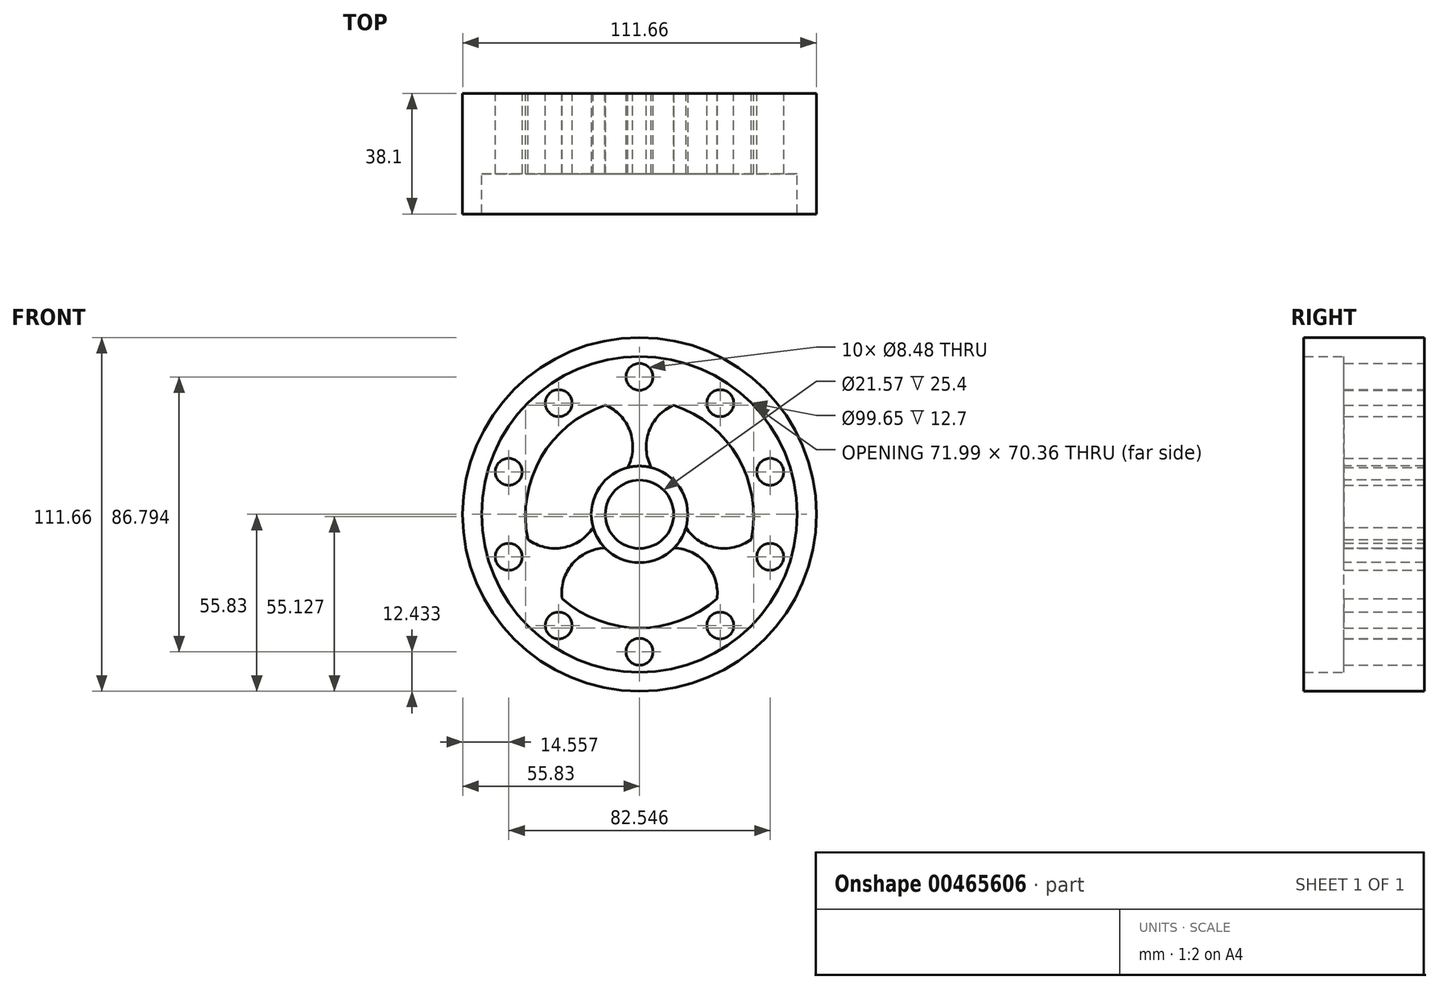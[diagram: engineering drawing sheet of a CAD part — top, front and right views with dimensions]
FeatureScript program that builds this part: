
annotation { "Feature Type Name" : "Feature", "Feature Type Description" : "" }
export const myFeature = defineFeature(function(context is Context, id is Id, definition is map)
    precondition{}
    {
        {
            var Q0;
            Q0=qCreatedBy(makeId("Front.planeOp"),FACE);
            var sketch = newSketch(context, id + "F0", { "sketchPlane" : qUnion([Q0])});
            skCircle(sketch, "E0", {"center": v(0, 0) * mm, "radius": 50.46 * mm});
            skCircle(sketch, "E1", {"center": v(0, 43.4) * mm, "radius": 4.24 * mm});
            skCircle(sketch, "E2.1.0", {"center": v(-25.5, 35.1) * mm, "radius": 4.24 * mm});
            skCircle(sketch, "E2.2.0", {"center": v(-41.27, 13.41) * mm, "radius": 4.24 * mm});
            skCircle(sketch, "E2.3.0", {"center": v(-41.27, -13.41) * mm, "radius": 4.24 * mm});
            skCircle(sketch, "E2.4.0", {"center": v(-25.5, -35.1) * mm, "radius": 4.24 * mm});
            skCircle(sketch, "E2.5.0", {"center": v(0, -43.4) * mm, "radius": 4.24 * mm});
            skCircle(sketch, "E2.6.0", {"center": v(25.5, -35.1) * mm, "radius": 4.24 * mm});
            skCircle(sketch, "E2.7.0", {"center": v(41.27, -13.41) * mm, "radius": 4.24 * mm});
            skCircle(sketch, "E2.8.0", {"center": v(41.27, 13.41) * mm, "radius": 4.24 * mm});
            skCircle(sketch, "E2.9.0", {"center": v(25.5, 35.1) * mm, "radius": 4.24 * mm});
            skArc(sketch, "E3", {"start": v(-3.72, 14.78) * mm, "mid": v(-2.95, 26.16) * mm, "end": v(-10.78, 34.48) * mm});
            skArc(sketch, "E4.MirrorCS", {"start": v(3.72, 14.78) * mm, "mid": v(2.95, 26.16) * mm, "end": v(10.78, 34.48) * mm});
            skCircle(sketch, "E5", {"center": v(0, 0) * mm, "radius": 15.24 * mm});
            skArc(sketch, "E6.1.0", {"start": v(-10.94, -10.6) * mm, "mid": v(-21.18, -15.64) * mm, "end": v(-24.47, -26.57) * mm});
            skArc(sketch, "E6.1.1", {"start": v(-14.65, -4.17) * mm, "mid": v(-24.14, -10.52) * mm, "end": v(-35.25, -7.9) * mm});
            skArc(sketch, "E6.2.0", {"start": v(14.65, -4.17) * mm, "mid": v(24.14, -10.52) * mm, "end": v(35.25, -7.9) * mm});
            skArc(sketch, "E6.2.1", {"start": v(10.94, -10.6) * mm, "mid": v(21.18, -15.64) * mm, "end": v(24.47, -26.57) * mm});
            skArc(sketch, "E7", {"start": v(-10.78, 34.48) * mm, "mid": v(-31.07, 17.94) * mm, "end": v(-35.25, -7.9) * mm});
            skArc(sketch, "E8.1.0", {"start": v(-24.47, -26.57) * mm, "mid": v(0, -35.88) * mm, "end": v(24.47, -26.57) * mm});
            skArc(sketch, "E8.2.0", {"start": v(35.25, -7.9) * mm, "mid": v(31.07, 17.94) * mm, "end": v(10.78, 34.48) * mm});
            skSolve(sketch);
        }
        {
            var Q0;
            Q0=makeQuery(id+"F0.imprint","IMPRINT",FACE,{"disambiguationData":[TD([[makeQuery(id+"F0.imprint","IMPRINT",EDGE,{"derivedFrom":sQuery(id+"F0.wireOp",EDGE,"E0")}),1.0]])]});
            extrude(context, id + "F1", {"entities" : qUnion([Q0]), "depth" : 25.4 * mm});
        }
        {
            var Q0;
            Q0=makeQuery(id+"F1.opExtrude","CAP_FACE",FACE,{"disambiguationData":[OSD([sQuery(id+"F0.wireOp",EDGE,"E0"),sQuery(id+"F0.wireOp",EDGE,"E1"),sQuery(id+"F0.wireOp",EDGE,"E2.1.0"),sQuery(id+"F0.wireOp",EDGE,"E2.2.0"),sQuery(id+"F0.wireOp",EDGE,"E2.3.0"),sQuery(id+"F0.wireOp",EDGE,"E2.4.0"),sQuery(id+"F0.wireOp",EDGE,"E2.5.0"),sQuery(id+"F0.wireOp",EDGE,"E2.6.0"),sQuery(id+"F0.wireOp",EDGE,"E2.7.0"),sQuery(id+"F0.wireOp",EDGE,"E2.8.0"),sQuery(id+"F0.wireOp",EDGE,"E2.9.0"),sQuery(id+"F0.wireOp",EDGE,"E3"),sQuery(id+"F0.wireOp",EDGE,"E4.MirrorCS"),sQuery(id+"F0.wireOp",EDGE,"E5"),sQuery(id+"F0.wireOp",EDGE,"E6.1.0"),sQuery(id+"F0.wireOp",EDGE,"E6.1.1"),sQuery(id+"F0.wireOp",EDGE,"E6.2.0"),sQuery(id+"F0.wireOp",EDGE,"E6.2.1"),sQuery(id+"F0.wireOp",EDGE,"E7"),sQuery(id+"F0.wireOp",EDGE,"E8.1.0"),sQuery(id+"F0.wireOp",EDGE,"E8.2.0")])],"isStart":false});
            var sketch = newSketch(context, id + "F2", { "sketchPlane" : qUnion([Q0])});
            skCircle(sketch, "E9", {"center": v(0, 0) * mm, "radius": 15.24 * mm});
            skCircle(sketch, "E10", {"center": v(0, 0) * mm, "radius": 10.78 * mm});
            skSolve(sketch);
        }
        {
            var Q0;
            Q0 = qSketchRegion(id + "F2", true);
            extrude(context, id + "F3", {"entities" : qUnion([Q0]), "oppositeDirection" : true, "depth" : 25.4 * mm});
        }
        {
            var Q0;
            Q0=qCreatedBy(makeId("Front.planeOp"),FACE);
            var sketch = newSketch(context, id + "F4", { "sketchPlane" : qUnion([Q0])});
            skCircle(sketch, "E11", {"center": v(0, 0) * mm, "radius": 55.83 * mm});
            skCircle(sketch, "E12", {"center": v(0, 0) * mm, "radius": 49.82 * mm});
            skSolve(sketch);
        }
        {
            var Q0;
            Q0=makeQuery(id+"F4.imprint","IMPRINT",FACE,{"disambiguationData":[TD([[makeQuery(id+"F4.imprint","IMPRINT",EDGE,{"derivedFrom":sQuery(id+"F4.wireOp",EDGE,"E11")}),1.0]])]});
            extrude(context, id + "F5", {"entities" : qUnion([Q0]), "operationType" : NewBodyOperationType.ADD, "depth" : 38.1 * mm});
        }
    });
